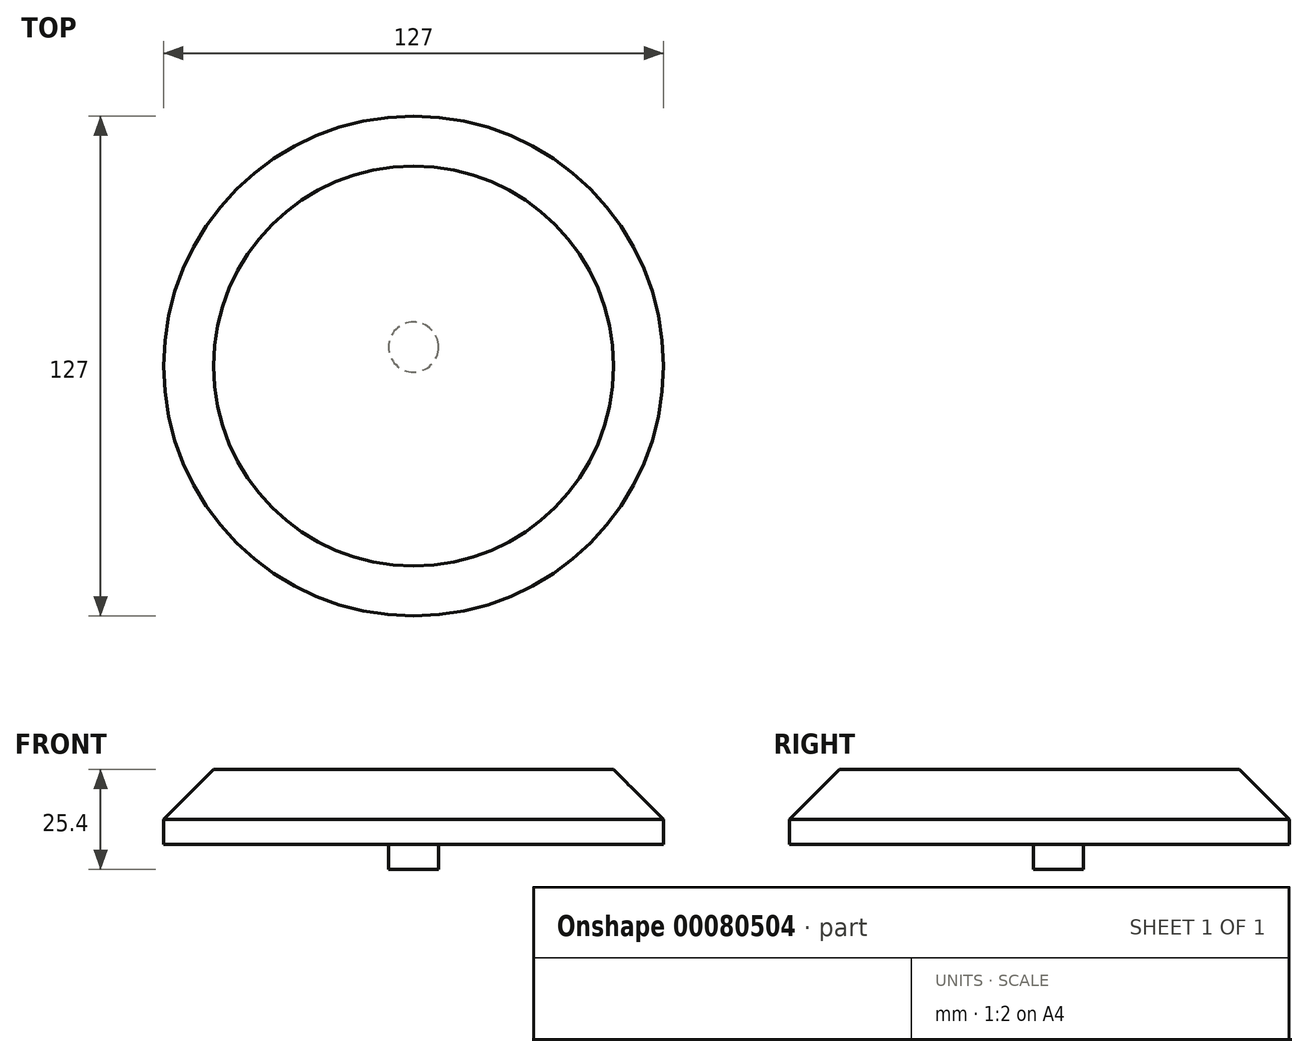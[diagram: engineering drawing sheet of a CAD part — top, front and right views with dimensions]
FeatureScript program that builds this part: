
annotation { "Feature Type Name" : "Feature", "Feature Type Description" : "" }
export const myFeature = defineFeature(function(context is Context, id is Id, definition is map)
    precondition{}
    {
        {
            var Q0;
            Q0=qCreatedBy(makeId("Top.planeOp"),FACE);
            var sketch = newSketch(context, id + "F0", { "sketchPlane" : qUnion([Q0])});
            skCircle(sketch, "E0", {"center": v(0, -4.81) * mm, "radius": 63.5 * mm});
            skSolve(sketch);
        }
        {
            var Q0;
            Q0 = qSketchRegion(id + "F0", true);
            extrude(context, id + "F1", {"entities" : qUnion([Q0]), "depth" : 19.05 * mm});
        }
        {
            var Q0;
            Q0=makeQuery(id+"F1.opExtrude","CAP_FACE",FACE,{"disambiguationData":[OSD([sQuery(id+"F0.wireOp",EDGE,"E0")])],"isStart":true});
            var sketch = newSketch(context, id + "F2", { "sketchPlane" : qUnion([Q0])});
            skCircle(sketch, "E1", {"center": v(0, 0) * mm, "radius": 6.35 * mm});
            skSolve(sketch);
        }
        {
            var Q0;
            Q0 = qSketchRegion(id + "F2", true);
            extrude(context, id + "F3", {"entities" : qUnion([Q0]), "operationType" : NewBodyOperationType.ADD, "depth" : 6.35 * mm});
        }
        {
            var Q0;
            Q0=makeQuery(id+"F1.opExtrude","CAP_EDGE",EDGE,{"disambiguationData":[OSD([sQuery(id+"F0.wireOp",EDGE,"E0")])],"isStart":false});
            chamfer(context, id + "F4", {"entities" : qUnion([Q0]), "width" : 12.7 * mm, "tangentPropagation" : true});
        }
    });
